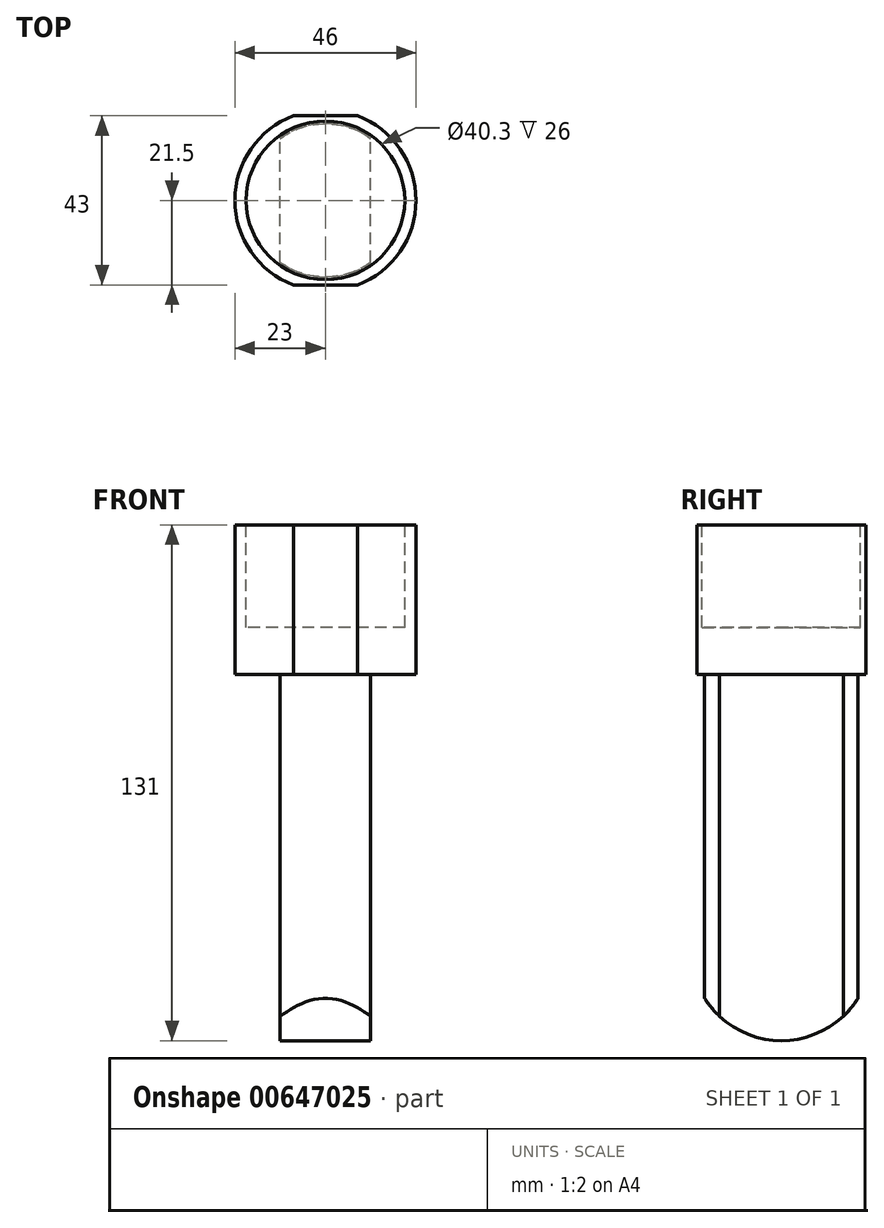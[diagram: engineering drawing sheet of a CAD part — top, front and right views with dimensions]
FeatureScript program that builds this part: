
annotation { "Feature Type Name" : "Feature", "Feature Type Description" : "" }
export const myFeature = defineFeature(function(context is Context, id is Id, definition is map)
    precondition{}
    {
        {
            var Q0;
            Q0=qCreatedBy(makeId("Top.planeOp"),FACE);
            var sketch = newSketch(context, id + "F0", { "sketchPlane" : qUnion([Q0])});
            skArc(sketch, "E0", {"start": v(-8.17, 21.5) * mm, "mid": v(-23, 0) * mm, "end": v(-8.17, -21.5) * mm});
            skLineSegment(sketch, "E1", {"start": v(-8.17, 21.5) * mm, "end": v(8.17, 21.5) * mm});
            skLineSegment(sketch, "E2.MirrorCS", {"start": v(-8.17, -21.5) * mm, "end": v(8.17, -21.5) * mm});
            skArc(sketch, "E3.trimOffspring", {"start": v(8.17, -21.5) * mm, "mid": v(23, 0) * mm, "end": v(8.17, 21.5) * mm});
            skSolve(sketch);
        }
        {
            var Q0;
            Q0=makeQuery(id+"F0.imprint","IMPRINT",FACE,{"disambiguationData":[TD([[makeQuery(id+"F0.imprint","IMPRINT",EDGE,{"derivedFrom":sQuery(id+"F0.wireOp",EDGE,"E0")}),1.0]])]});
            extrude(context, id + "F1", {"entities" : qUnion([Q0]), "depth" : 38 * mm, "offsetDistance" : 25 * mm});
        }
        {
            var Q0;
            Q0=makeQuery(id+"F1.opExtrude","CAP_FACE",FACE,{"disambiguationData":[OSD([sQuery(id+"F0.wireOp",EDGE,"E0"),sQuery(id+"F0.wireOp",EDGE,"E1"),sQuery(id+"F0.wireOp",EDGE,"E2.MirrorCS"),sQuery(id+"F0.wireOp",EDGE,"E3.trimOffspring")])],"isStart":false});
            var sketch = newSketch(context, id + "F2", { "sketchPlane" : qUnion([Q0])});
            skCircle(sketch, "E4", {"center": v(0, 0) * mm, "radius": 20.15 * mm});
            skSolve(sketch);
        }
        {
            var Q0;
            Q0=makeQuery(id+"F2.imprint","IMPRINT",FACE,{"disambiguationData":[TD([[makeQuery(id+"F2.imprint","IMPRINT",EDGE,{"derivedFrom":sQuery(id+"F2.wireOp",EDGE,"E4")}),1.0]])]});
            extrude(context, id + "F3", {"entities" : qUnion([Q0]), "operationType" : NewBodyOperationType.REMOVE, "oppositeDirection" : true, "depth" : 26 * mm, "offsetDistance" : 25 * mm});
        }
        {
            var Q0;
            Q0=makeQuery(id+"F1.opExtrude","CAP_FACE",FACE,{"disambiguationData":[OSD([sQuery(id+"F0.wireOp",EDGE,"E0"),sQuery(id+"F0.wireOp",EDGE,"E1"),sQuery(id+"F0.wireOp",EDGE,"E2.MirrorCS"),sQuery(id+"F0.wireOp",EDGE,"E3.trimOffspring")])],"isStart":true});
            var sketch = newSketch(context, id + "F4", { "sketchPlane" : qUnion([Q0])});
            skArc(sketch, "E5", {"start": v(-11.5, -15.75) * mm, "mid": v(0, -19.5) * mm, "end": v(11.5, -15.75) * mm});
            skLineSegment(sketch, "E6", {"start": v(-11.5, 15.75) * mm, "end": v(-11.5, -15.75) * mm});
            skLineSegment(sketch, "E7.MirrorCS", {"start": v(11.5, 15.75) * mm, "end": v(11.5, -15.75) * mm});
            skArc(sketch, "E8.trimOffspring", {"start": v(11.5, 15.75) * mm, "mid": v(0, 19.5) * mm, "end": v(-11.5, 15.75) * mm});
            skSolve(sketch);
        }
        {
            var Q0;
            Q0=makeQuery(id+"F4.imprint","IMPRINT",FACE,{"disambiguationData":[TD([[makeQuery(id+"F4.imprint","IMPRINT",EDGE,{"derivedFrom":sQuery(id+"F4.wireOp",EDGE,"E5")}),1.0]])]});
            extrude(context, id + "F5", {"entities" : qUnion([Q0]), "operationType" : NewBodyOperationType.ADD, "depth" : 93 * mm, "offsetDistance" : 25 * mm});
        }
        {
            var Q0;
            Q0=makeQuery(id+"F5.opExtrude","SWEPT_FACE",FACE,{"disambiguationData":[OSD([sQuery(id+"F4.wireOp",EDGE,"E7.MirrorCS")])]});
            var sketch = newSketch(context, id + "F6", { "sketchPlane" : qUnion([Q0])});
            skCircle(sketch, "E9", {"center": v(0, -70) * mm, "radius": 23 * mm});
            skLineSegment(sketch, "E10", {"start": v(-22.5, -74.77) * mm, "end": v(-28.7, -107.15) * mm});
            skLineSegment(sketch, "E11", {"start": v(-28.7, -107.15) * mm, "end": v(29.35, -107.15) * mm});
            skLineSegment(sketch, "E12", {"start": v(29.35, -107.15) * mm, "end": v(22.41, -75.17) * mm});
            skSolve(sketch);
        }
        {
            var Q0;
            {var subQ5=sQuery(id+"F6.wireOp",EDGE,"E10");Q0=makeQuery(id+"F6.imprint","IMPRINT",FACE,{"disambiguationData":[TD([[makeQuery(id+"F6.imprint","IMPRINT",EDGE,{"derivedFrom":subQ5}),1.0]])]});}
            var Q1;
            {var subQ0=sQuery(id+"F6.wireOp",EDGE,"E9");var subQ1=sQuery(id+"F4.wireOp",EDGE,"E7.MirrorCS");var subQ4=makeQuery(id+"F5.opExtrude","CAP_EDGE",EDGE,{"disambiguationData":[OSD([subQ1])],"isStart":false});var subQ5=makeQuery(id+"F6.imprint","INTERSECT",VERTEX,{"derivedFrom":[subQ4,subQ0]});Q1=makeQuery(id+"F6.imprint","IMPRINT",FACE,{"disambiguationData":[TD([[makeQuery(id+"F6.imprint","IMPRINT",EDGE,{"disambiguationData":[TD([[subQ5,1.0]])],"derivedFrom":subQ0}),-1.0]])]});}
            var Q2;
            {var subQ0=sQuery(id+"F6.wireOp",EDGE,"E9");var subQ1=sQuery(id+"F4.wireOp",EDGE,"E7.MirrorCS");var subQ2=makeQuery(id+"F5.opExtrude","CAP_EDGE",EDGE,{"disambiguationData":[OSD([subQ1])],"isStart":false});var subQ3=makeQuery(id+"F6.imprint","INTERSECT",VERTEX,{"derivedFrom":[subQ2,subQ0]});Q2=makeQuery(id+"F6.imprint","IMPRINT",FACE,{"disambiguationData":[TD([[makeQuery(id+"F6.imprint","IMPRINT",EDGE,{"disambiguationData":[TD([[subQ3,-1.0]])],"derivedFrom":subQ0}),-1.0]])]});}
            extrude(context, id + "F7", {"entities" : qUnion([Q0, Q1, Q2]), "operationType" : NewBodyOperationType.REMOVE, "endBound" : BoundingType.THROUGH_ALL, "oppositeDirection" : true, "depth" : 25 * mm, "offsetDistance" : 25 * mm});
        }
    });
